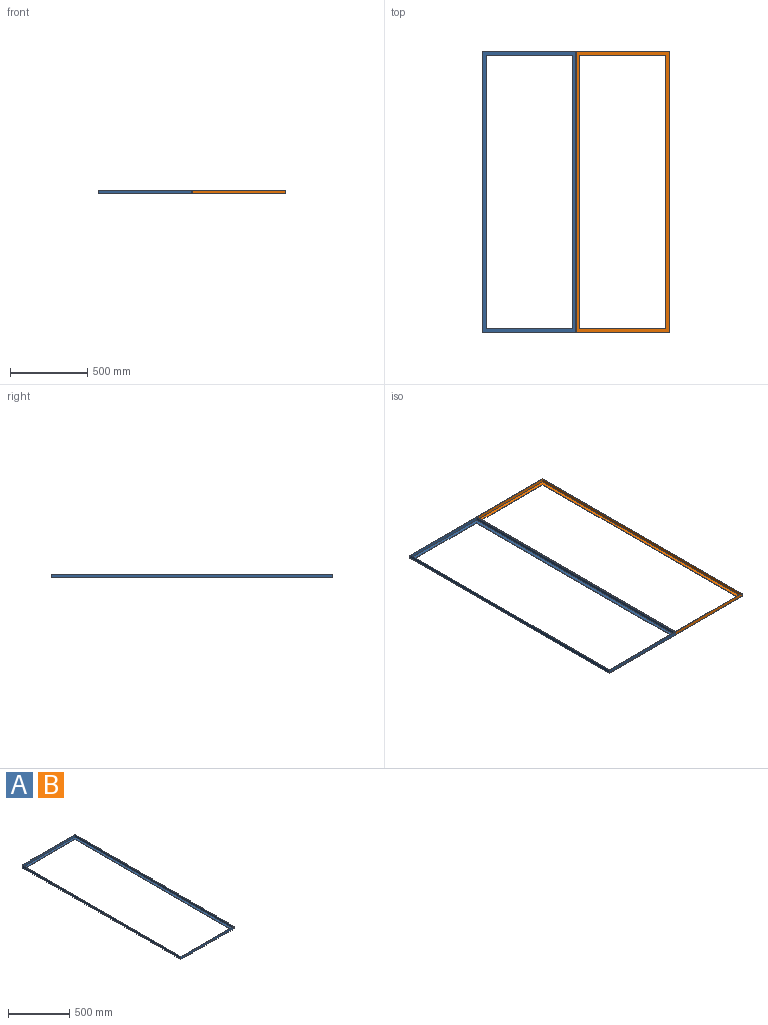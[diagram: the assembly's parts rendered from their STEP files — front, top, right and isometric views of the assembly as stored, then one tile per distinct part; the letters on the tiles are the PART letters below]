
ASSEMBLY  parts=2 mates=1
PART A: 15 faces, bbox 609.6x1828.8x25.4 mm
  f0: plane 1828.8x609.6mm, normal (0,0,1), area 15443.5mm2, adj f1,f2,f3,f4,f6,f7,f8,f9
  f1: plane 609.6x25.4mm, normal (0,-1,0), area 15483.8mm2, adj f0,f2,f4,f5
  f2: plane 1828.8x25.4mm, normal (1,0,0), area 46451.5mm2, adj f0,f1,f3,f5
  f3: plane 609.6x25.4mm, normal (0,1,0), area 15483.8mm2, adj f0,f2,f4,f5
  f4: plane 1828.8x25.4mm, normal (-1,0,0), area 46451.5mm2, adj f0,f1,f3,f5
  f5: plane 1828.8x609.6mm, normal (0,0,-1), area 121290.1mm2, adj f1,f2,f3,f4,f11,f12,f13,f14
  f6: plane 603.25x22.23mm, normal (0,1,0), area 13407.2mm2, adj f0,f7,f9,f10
  f7: plane 1822.45x22.23mm, normal (-1,0,0), area 40504mm2, adj f0,f6,f8,f10
  f8: plane 603.25x22.23mm, normal (0,-1,0), area 13407.2mm2, adj f0,f7,f9,f10
  f9: plane 1822.45x22.23mm, normal (1,0,0), area 40504mm2, adj f0,f6,f8,f10
  f10: plane 1822.45x603.25mm, normal (0,0,1), area 105846.6mm2, adj f6,f7,f8,f9,f11,f12,f13,f14
  f11: plane 558.8x3.18mm, normal (0,1,0), area 1774.2mm2, adj f5,f10,f12,f14
  f12: plane 1778x3.18mm, normal (1,0,0), area 5645.1mm2, adj f5,f10,f11,f13
  f13: plane 558.8x3.18mm, normal (0,-1,0), area 1774.2mm2, adj f5,f10,f12,f14
  f14: plane 1778x3.18mm, normal (-1,0,0), area 5645.1mm2, adj f5,f10,f11,f13
PART B: same geometry as A
PLACE A at identity
PLACE B t=(609.6,0,0)mm
MATE planar B.f1 <-> A.f1  axis (0,-1,0) through (304.8,-914.4,0)mm
